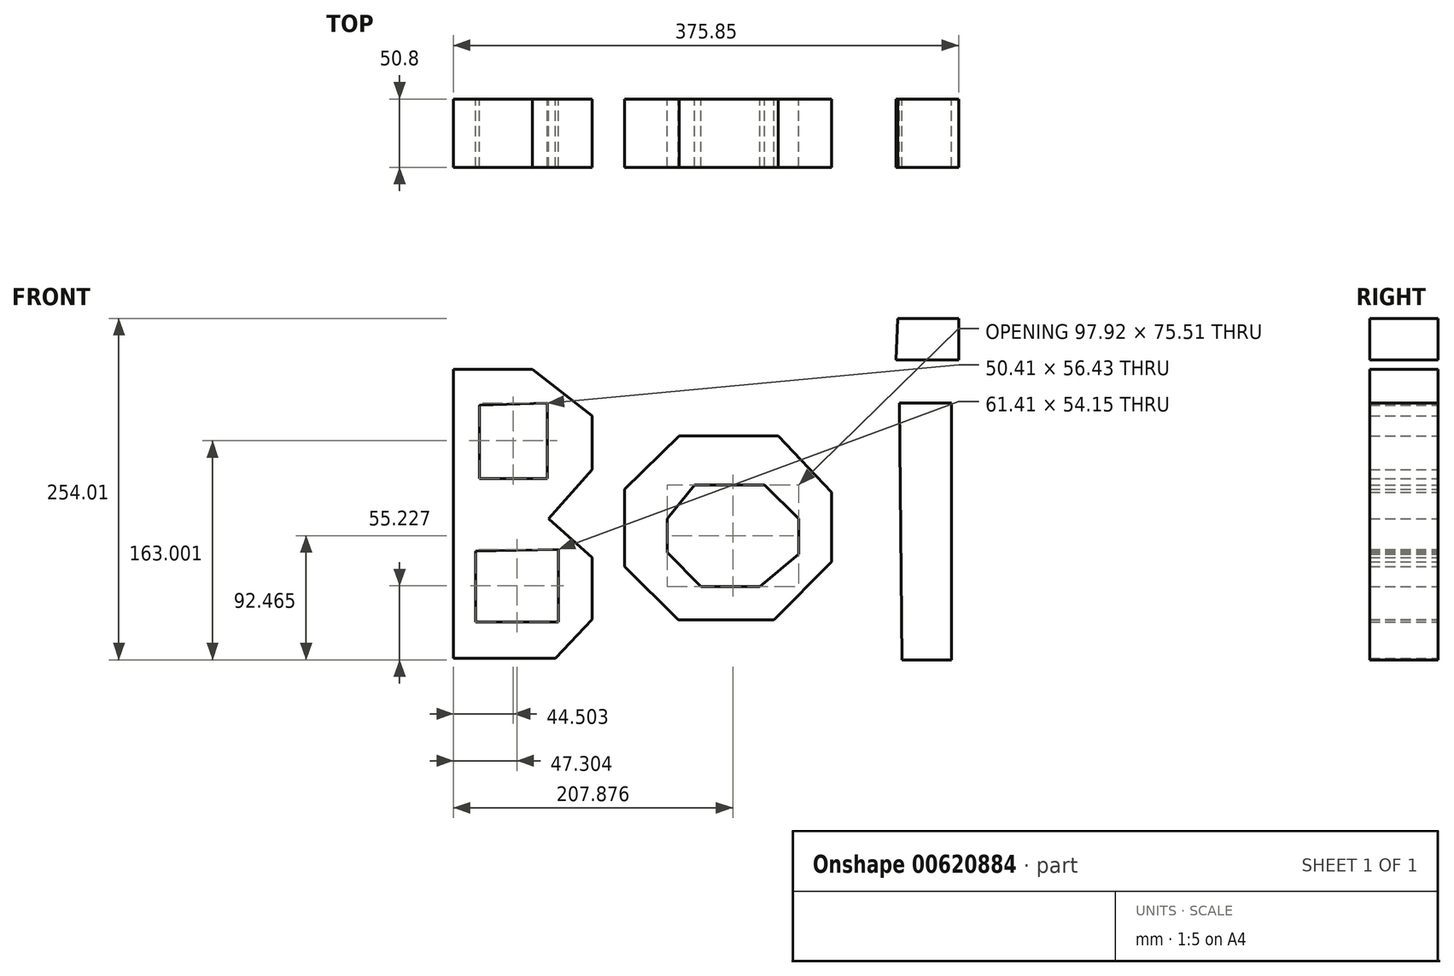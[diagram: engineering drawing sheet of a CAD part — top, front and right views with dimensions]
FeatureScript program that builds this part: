
annotation { "Feature Type Name" : "Feature", "Feature Type Description" : "" }
export const myFeature = defineFeature(function(context is Context, id is Id, definition is map)
    precondition{}
    {
        {
            var Q0;
            Q0=qCreatedBy(makeId("Front.planeOp"),FACE);
            var sketch = newSketch(context, id + "F0", { "sketchPlane" : qUnion([Q0])});
            skLineSegment(sketch, "E0", {"start": v(-103.1, 110.99) * mm, "end": v(-103.1, -103.94) * mm});
            skLineSegment(sketch, "E1", {"start": v(-103.1, -103.94) * mm, "end": v(-27.38, -103.94) * mm});
            skLineSegment(sketch, "E2", {"start": v(-27.38, -103.94) * mm, "end": v(0, -74.9) * mm});
            skLineSegment(sketch, "E3", {"start": v(0, -74.9) * mm, "end": v(0, -28.84) * mm});
            skLineSegment(sketch, "E4", {"start": v(0, -28.84) * mm, "end": v(-32.36, 0) * mm});
            skLineSegment(sketch, "E5", {"start": v(-32.36, 0) * mm, "end": v(-103.1, 0) * mm});
            skPoint(sketch, "E5.endSnap0", {"position": v(-103.1, 3.53) * mm});
            skLineSegment(sketch, "E6", {"start": v(-103.1, 0) * mm, "end": v(-32.36, 0) * mm});
            skLineSegment(sketch, "E7", {"start": v(-32.36, 0) * mm, "end": v(0, 36.32) * mm});
            skLineSegment(sketch, "E8", {"start": v(0, 36.32) * mm, "end": v(0, 76.34) * mm});
            skLineSegment(sketch, "E9", {"start": v(0, 76.34) * mm, "end": v(-44.4, 110.99) * mm});
            skLineSegment(sketch, "E10", {"start": v(-44.4, 110.99) * mm, "end": v(-103.1, 110.99) * mm});
            skLineSegment(sketch, "E11", {"start": v(-83.81, 84.44) * mm, "end": v(-83.81, 29.67) * mm});
            skLineSegment(sketch, "E12", {"start": v(-83.81, 29.67) * mm, "end": v(-33.4, 29.67) * mm});
            skLineSegment(sketch, "E13", {"start": v(-33.4, 29.67) * mm, "end": v(-33.4, 86.1) * mm});
            skLineSegment(sketch, "E14", {"start": v(-33.4, 86.1) * mm, "end": v(-83.81, 84.44) * mm});
            skLineSegment(sketch, "E15", {"start": v(-86.5, -24.27) * mm, "end": v(-86.5, -76.97) * mm});
            skLineSegment(sketch, "E16", {"start": v(-86.5, -76.97) * mm, "end": v(-25.1, -76.97) * mm});
            skLineSegment(sketch, "E17", {"start": v(-25.1, -76.97) * mm, "end": v(-25.1, -22.82) * mm});
            skLineSegment(sketch, "E18", {"start": v(-25.1, -22.82) * mm, "end": v(-86.5, -24.27) * mm});
            skLineSegment(sketch, "E19", {"start": v(64.1, -75.3) * mm, "end": v(135.47, -75.3) * mm});
            skLineSegment(sketch, "E20", {"start": v(135.47, -75.3) * mm, "end": v(178.2, -32.16) * mm});
            skLineSegment(sketch, "E21", {"start": v(178.2, -32.16) * mm, "end": v(178.2, 19.7) * mm});
            skLineSegment(sketch, "E22", {"start": v(178.2, 19.7) * mm, "end": v(138.37, 61.4) * mm});
            skLineSegment(sketch, "E23", {"start": v(138.37, 61.4) * mm, "end": v(64.73, 61.4) * mm});
            skLineSegment(sketch, "E24", {"start": v(64.73, 61.4) * mm, "end": v(24.27, 22) * mm});
            skLineSegment(sketch, "E25", {"start": v(24.27, 22) * mm, "end": v(24.27, -35.48) * mm});
            skLineSegment(sketch, "E26", {"start": v(24.27, -35.48) * mm, "end": v(64.1, -75.3) * mm});
            skLineSegment(sketch, "E27", {"start": v(76.14, 25.1) * mm, "end": v(128.42, 25.1) * mm});
            skLineSegment(sketch, "E28", {"start": v(128.42, 25.1) * mm, "end": v(153.73, 0) * mm});
            skLineSegment(sketch, "E29", {"start": v(153.73, 0) * mm, "end": v(153.73, -26.35) * mm});
            skLineSegment(sketch, "E30", {"start": v(153.73, -26.35) * mm, "end": v(124.89, -50.41) * mm});
            skLineSegment(sketch, "E31", {"start": v(124.89, -50.41) * mm, "end": v(81.12, -50.41) * mm});
            skLineSegment(sketch, "E32", {"start": v(81.12, -50.41) * mm, "end": v(55.8, -25.3) * mm});
            skLineSegment(sketch, "E33", {"start": v(55.8, -25.3) * mm, "end": v(55.8, 0) * mm});
            skLineSegment(sketch, "E34", {"start": v(55.8, 0) * mm, "end": v(76.14, 25.1) * mm});
            skLineSegment(sketch, "E35", {"start": v(228.56, 85.9) * mm, "end": v(267.37, 85.9) * mm});
            skLineSegment(sketch, "E36", {"start": v(267.37, 85.9) * mm, "end": v(267.37, -105.12) * mm});
            skLineSegment(sketch, "E37", {"start": v(267.37, -105.12) * mm, "end": v(230.65, -105.12) * mm});
            skLineSegment(sketch, "E38", {"start": v(230.65, -105.12) * mm, "end": v(228.56, 85.9) * mm});
            skLineSegment(sketch, "E39", {"start": v(227.37, 148.89) * mm, "end": v(272.74, 148.89) * mm});
            skLineSegment(sketch, "E40", {"start": v(272.74, 148.89) * mm, "end": v(272.74, 118.15) * mm});
            skLineSegment(sketch, "E41", {"start": v(272.74, 118.15) * mm, "end": v(226.18, 118.15) * mm});
            skLineSegment(sketch, "E42", {"start": v(226.18, 118.15) * mm, "end": v(227.37, 148.89) * mm});
            skSolve(sketch);
        }
        {
            var Q0;
            Q0 = qSketchRegion(id + "F0", true);
            extrude(context, id + "F1", {"entities" : qUnion([Q0]), "depth" : 50.8 * mm, "offsetDistance" : 25.4 * mm});
        }
    });
